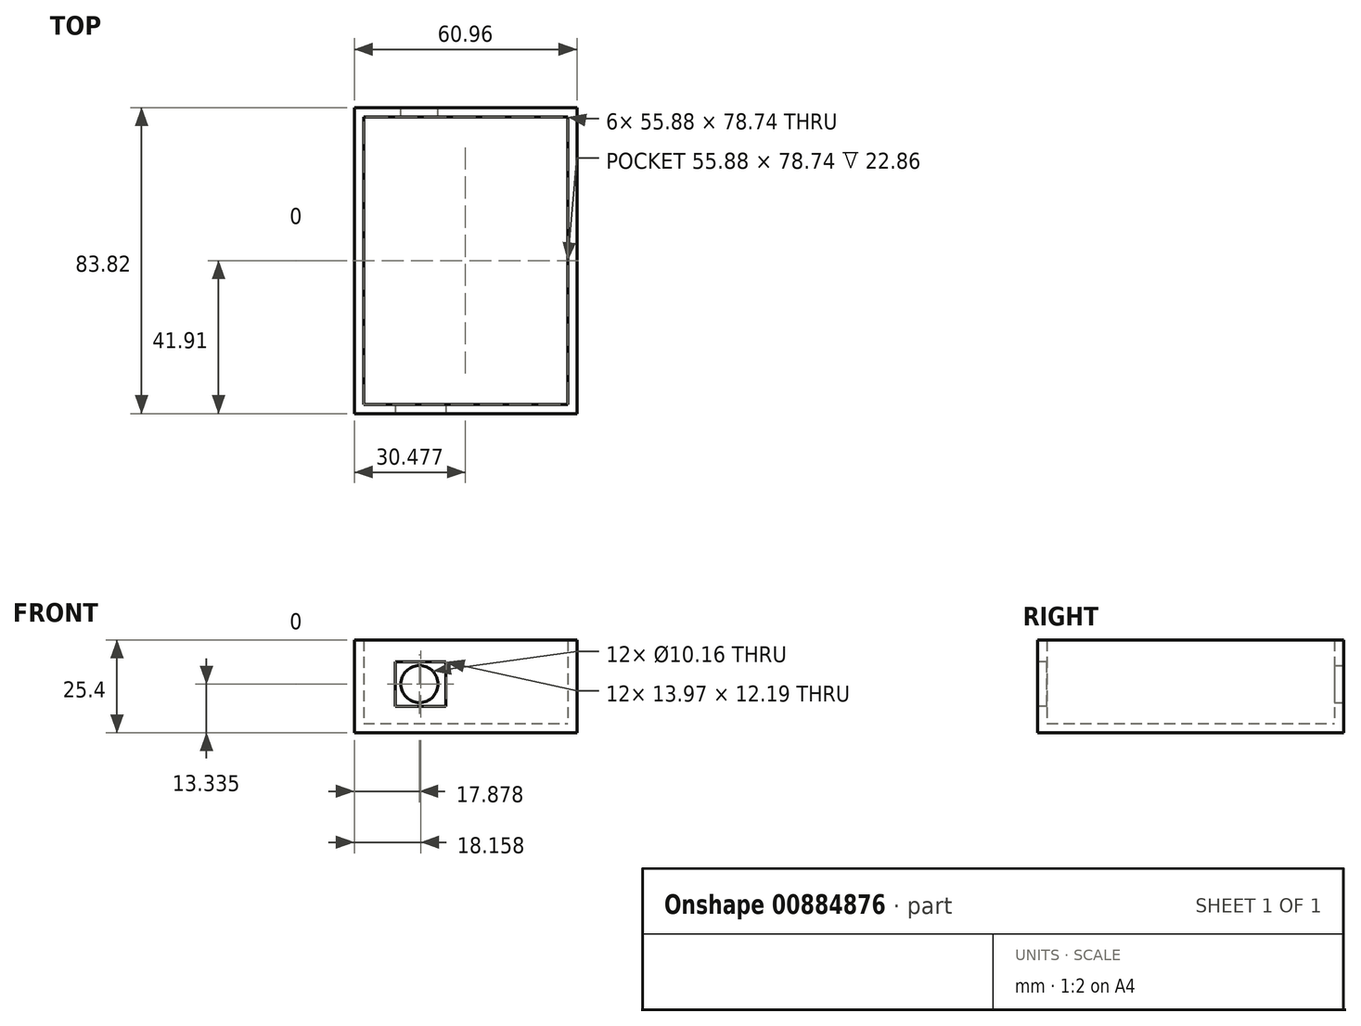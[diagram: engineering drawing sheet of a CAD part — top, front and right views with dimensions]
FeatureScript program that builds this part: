
annotation { "Feature Type Name" : "Feature", "Feature Type Description" : "" }
export const myFeature = defineFeature(function(context is Context, id is Id, definition is map)
    precondition{}
    {
        {
            var Q0;
            Q0=qCreatedBy(makeId("Top.planeOp"),FACE);
            var sketch = newSketch(context, id + "F0", { "sketchPlane" : qUnion([Q0])});
            skLineSegment(sketch, "E0.bottom", {"start": v(-39.64, -57.15) * mm, "end": v(21.32, -57.15) * mm});
            skLineSegment(sketch, "E0.top", {"start": v(-39.64, 26.67) * mm, "end": v(21.32, 26.67) * mm});
            skLineSegment(sketch, "E0.left", {"start": v(-39.64, -57.15) * mm, "end": v(-39.64, 26.67) * mm});
            skLineSegment(sketch, "E0.right", {"start": v(21.32, -57.15) * mm, "end": v(21.32, 26.67) * mm});
            skPoint(sketch, "E0.middle", {"position": v(-3.81, 0) * mm});
            skSolve(sketch);
        }
        {
            var Q0;
            Q0=makeQuery(id+"F0.imprint","IMPRINT",FACE,{"disambiguationData":[TD([[makeQuery(id+"F0.imprint","IMPRINT",EDGE,{"derivedFrom":sQuery(id+"F0.wireOp",EDGE,"E0.bottom")}),1.0]])]});
            extrude(context, id + "F1", {"entities" : qUnion([Q0]), "depth" : 25.4 * mm, "offsetDistance" : 25.4 * mm});
        }
        {
            var Q0;
            Q0=makeQuery(id+"F1.opExtrude","CAP_FACE",FACE,{"disambiguationData":[OSD([sQuery(id+"F0.wireOp",EDGE,"E0.bottom"),sQuery(id+"F0.wireOp",EDGE,"E0.top"),sQuery(id+"F0.wireOp",EDGE,"E0.left"),sQuery(id+"F0.wireOp",EDGE,"E0.right")])],"isStart":false});
            shell(context, id + "F2", {"entities" : qUnion([Q0]), "thickness" : 2.54 * mm});
        }
        {
            var Q0;
            Q0=makeQuery(id+"F1.opExtrude","SWEPT_FACE",FACE,{"disambiguationData":[OSD([sQuery(id+"F0.wireOp",EDGE,"E0.bottom")])]});
            var sketch = newSketch(context, id + "F3", { "sketchPlane" : qUnion([Q0])});
            skLineSegment(sketch, "E1.bottom", {"start": v(-14.5, 7.24) * mm, "end": v(-28.47, 7.24) * mm});
            skLineSegment(sketch, "E1.top", {"start": v(-14.5, 19.43) * mm, "end": v(-28.47, 19.43) * mm});
            skLineSegment(sketch, "E1.left", {"start": v(-14.5, 7.24) * mm, "end": v(-14.5, 19.43) * mm});
            skLineSegment(sketch, "E1.right", {"start": v(-28.47, 7.24) * mm, "end": v(-28.47, 19.43) * mm});
            skPoint(sketch, "E1.middle", {"position": v(-21.48, 13.34) * mm});
            skPoint(sketch, "E1.cornerSnap0", {"position": v(-14.5, 0) * mm});
            skSolve(sketch);
        }
        {
            var Q0;
            Q0=makeQuery(id+"F3.imprint","IMPRINT",FACE,{"disambiguationData":[TD([[makeQuery(id+"F3.imprint","IMPRINT",EDGE,{"derivedFrom":sQuery(id+"F3.wireOp",EDGE,"E1.bottom")}),-1.0]])]});
            extrude(context, id + "F4", {"entities" : qUnion([Q0]), "operationType" : NewBodyOperationType.REMOVE, "endBound" : BoundingType.UP_TO_NEXT, "oppositeDirection" : true, "depth" : 2.3 * mm, "offsetDistance" : 25.4 * mm});
        }
        {
            var Q0;
            Q0=makeQuery(id+"F1.opExtrude","SWEPT_FACE",FACE,{"disambiguationData":[OSD([sQuery(id+"F0.wireOp",EDGE,"E0.top")])]});
            var sketch = newSketch(context, id + "F5", { "sketchPlane" : qUnion([Q0])});
            skCircle(sketch, "E2", {"center": v(21.76, 13.34) * mm, "radius": 5.08 * mm});
            skCircle(sketch, "E3", {"center": v(21.76, 13.34) * mm, "radius": 12.07 * mm});
            skSolve(sketch);
        }
        {
            var Q0;
            Q0=makeQuery(id+"F5.imprint","IMPRINT",FACE,{"disambiguationData":[TD([[makeQuery(id+"F5.imprint","IMPRINT",EDGE,{"derivedFrom":sQuery(id+"F5.wireOp",EDGE,"E2")}),1.0]])]});
            extrude(context, id + "F6", {"entities" : qUnion([Q0]), "operationType" : NewBodyOperationType.REMOVE, "endBound" : BoundingType.UP_TO_NEXT, "oppositeDirection" : true, "depth" : 25.4 * mm, "offsetDistance" : 25.4 * mm});
        }
    });
